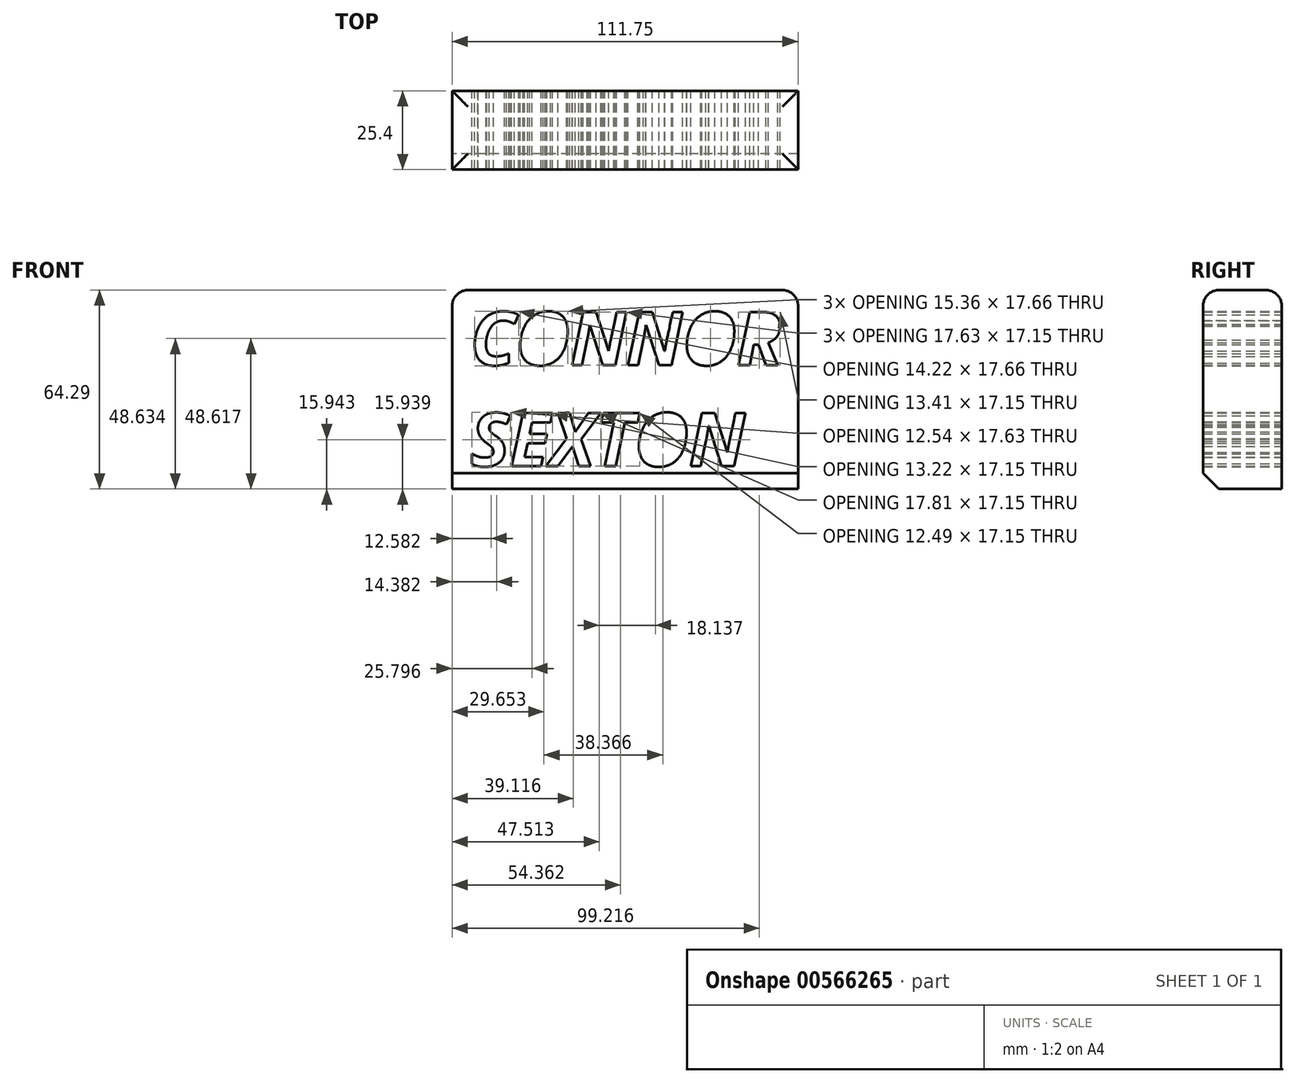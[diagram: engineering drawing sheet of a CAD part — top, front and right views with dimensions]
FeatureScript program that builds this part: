
annotation { "Feature Type Name" : "Feature", "Feature Type Description" : "" }
export const myFeature = defineFeature(function(context is Context, id is Id, definition is map)
    precondition{}
    {
        {
            var Q0;
            Q0=qCreatedBy(makeId("Front.planeOp"),FACE);
            var sketch = newSketch(context, id + "F0", { "sketchPlane" : qUnion([Q0])});
            skLineSegment(sketch, "E0.bottom", {"start": v(-111.75, 64.29) * mm, "end": v(0, 64.29) * mm});
            skLineSegment(sketch, "E0.top", {"start": v(-111.75, 0) * mm, "end": v(0, 0) * mm});
            skLineSegment(sketch, "E0.left", {"start": v(-111.75, 64.29) * mm, "end": v(-111.75, 0) * mm});
            skLineSegment(sketch, "E0.right", {"start": v(0, 64.29) * mm, "end": v(0, 0) * mm});
            skText(sketch, "E1", { "text": "CONNOR\nSEXTON", "fontName": "OpenSans-BoldItalic.ttf"});
            const initialGuessF0  = {"E1": [-0.10592, 0.04004, 1, 0, 0.0173]};
            skSetInitialGuess(sketch, initialGuessF0);
            skSolve(sketch);
        }
        {
            var Q0;
            Q0=makeQuery(id+"F0.imprint","IMPRINT",FACE,{"disambiguationData":[TD([[makeQuery(id+"F0.imprint","IMPRINT",EDGE,{"derivedFrom":sQuery(id+"F0.wireOp",EDGE,"E0.bottom")}),-1.0]])]});
            extrude(context, id + "F1", {"entities" : qUnion([Q0]), "depth" : 25.4 * mm, "offsetDistance" : 25.4 * mm});
        }
        {
            var Q0;
            Q0=makeQuery(id+"F1.opExtrude","CAP_EDGE",EDGE,{"disambiguationData":[OSD([sQuery(id+"F0.wireOp",EDGE,"E0.bottom")])],"isStart":false});
            var Q1;
            Q1=makeQuery(id+"F1.opExtrude","CAP_EDGE",EDGE,{"disambiguationData":[OSD([sQuery(id+"F0.wireOp",EDGE,"E0.bottom")])],"isStart":true});
            var Q2;
            Q2=makeQuery(id+"F1.opExtrude","SWEPT_EDGE",EDGE,{"disambiguationData":[OSD([sQuery(id+"F0.wireOp",EDGE,"E0.bottom"),sQuery(id+"F0.wireOp",EDGE,"E0.right")])]});
            var Q3;
            Q3=makeQuery(id+"F1.opExtrude","SWEPT_EDGE",EDGE,{"disambiguationData":[OSD([sQuery(id+"F0.wireOp",EDGE,"E0.bottom"),sQuery(id+"F0.wireOp",EDGE,"E0.left")])]});
            fillet(context, id + "F2", {"entities" : qUnion([Q0, Q1, Q2, Q3]), "radius" : 5.08 * mm, "tangentPropagation" : true, "allowEdgeOverflow" : false});
        }
        {
            var Q0;
            Q0=makeQuery(id+"F1.opExtrude","CAP_EDGE",EDGE,{"disambiguationData":[OSD([sQuery(id+"F0.wireOp",EDGE,"E0.top")])],"isStart":false});
            chamfer(context, id + "F3", {"entities" : qUnion([Q0]), "width" : 5.08 * mm, "tangentPropagation" : true});
        }
    });
